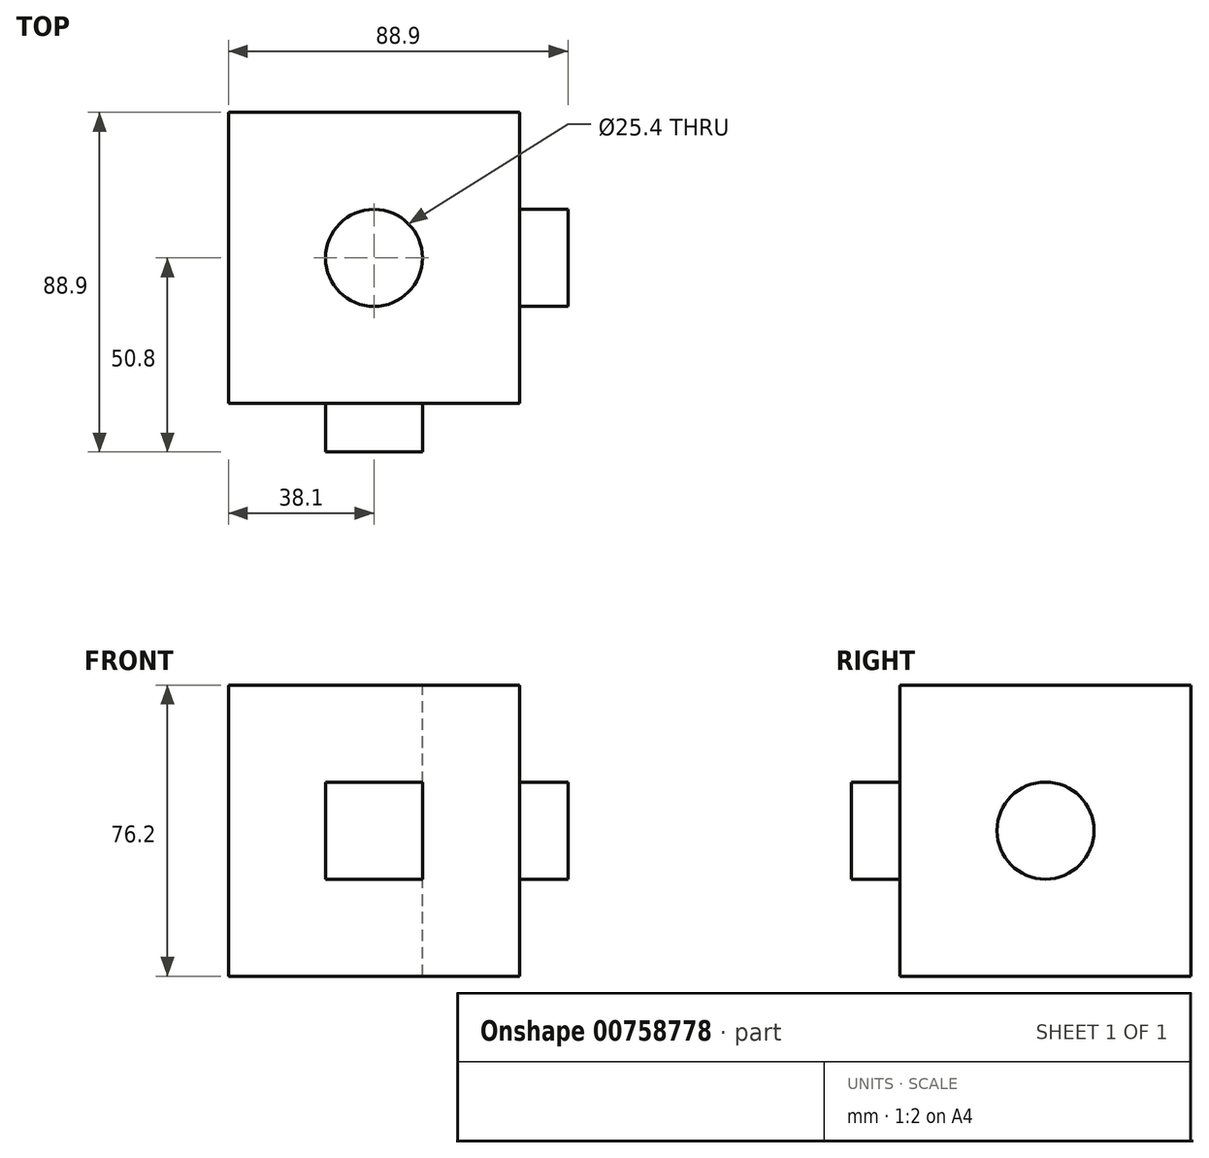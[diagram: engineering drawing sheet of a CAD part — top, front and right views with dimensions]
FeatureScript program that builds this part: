
annotation { "Feature Type Name" : "Feature", "Feature Type Description" : "" }
export const myFeature = defineFeature(function(context is Context, id is Id, definition is map)
    precondition{}
    {
        {
            var Q0;
            Q0=qCreatedBy(makeId("Front.planeOp"),FACE);
            var sketch = newSketch(context, id + "F0", { "sketchPlane" : qUnion([Q0])});
            skLineSegment(sketch, "E0.bottom", {"start": v(-36.95, 54.33) * mm, "end": v(39.25, 54.33) * mm});
            skLineSegment(sketch, "E0.top", {"start": v(-36.95, -21.87) * mm, "end": v(39.25, -21.87) * mm});
            skLineSegment(sketch, "E0.left", {"start": v(-36.95, 54.33) * mm, "end": v(-36.95, -21.87) * mm});
            skLineSegment(sketch, "E0.right", {"start": v(39.25, 54.33) * mm, "end": v(39.25, -21.87) * mm});
            skLineSegment(sketch, "E1.bottom", {"start": v(39.25, -21.87) * mm, "end": v(42.06, -21.87) * mm});
            skLineSegment(sketch, "E1.top", {"start": v(39.25, -18.33) * mm, "end": v(42.06, -18.33) * mm});
            skLineSegment(sketch, "E1.left", {"start": v(39.25, -21.87) * mm, "end": v(39.25, -18.33) * mm});
            skLineSegment(sketch, "E1.right", {"start": v(42.06, -21.87) * mm, "end": v(42.06, -18.33) * mm});
            skSolve(sketch);
        }
        {
            var Q0;
            Q0=makeQuery(id+"F0.imprint","IMPRINT",FACE,{"disambiguationData":[TD([[makeQuery(id+"F0.imprint","IMPRINT",EDGE,{"derivedFrom":sQuery(id+"F0.wireOp",EDGE,"E0.bottom")}),-1.0]])]});
            extrude(context, id + "F1", {"entities" : qUnion([Q0]), "depth" : 76.2 * mm, "offsetDistance" : 25.4 * mm});
        }
        {
            var Q0;
            Q0=makeQuery(id+"F1.opExtrude","CAP_FACE",FACE,{"disambiguationData":[OSD([sQuery(id+"F0.wireOp",EDGE,"E0.bottom"),sQuery(id+"F0.wireOp",EDGE,"E0.top"),sQuery(id+"F0.wireOp",EDGE,"E0.left"),sQuery(id+"F0.wireOp",EDGE,"E0.right"),sQuery(id+"F0.wireOp",EDGE,"E1.left")])],"isStart":false});
            var sketch = newSketch(context, id + "F2", { "sketchPlane" : qUnion([Q0])});
            skLineSegment(sketch, "E2.bottom", {"start": v(-11.55, 28.93) * mm, "end": v(13.85, 28.93) * mm});
            skLineSegment(sketch, "E2.top", {"start": v(-11.55, 3.53) * mm, "end": v(13.85, 3.53) * mm});
            skLineSegment(sketch, "E2.left", {"start": v(-11.55, 28.93) * mm, "end": v(-11.55, 3.53) * mm});
            skLineSegment(sketch, "E2.right", {"start": v(13.85, 28.93) * mm, "end": v(13.85, 3.53) * mm});
            skSolve(sketch);
        }
        {
            var Q0;
            Q0=makeQuery(id+"F2.imprint","IMPRINT",FACE,{"disambiguationData":[TD([[makeQuery(id+"F2.imprint","IMPRINT",EDGE,{"derivedFrom":sQuery(id+"F2.wireOp",EDGE,"E2.bottom")}),-1.0]])]});
            extrude(context, id + "F3", {"entities" : qUnion([Q0]), "operationType" : NewBodyOperationType.ADD, "depth" : 12.7 * mm, "offsetDistance" : 25.4 * mm});
        }
        {
            var Q0;
            Q0=makeQuery(id+"F1.opExtrude","SWEPT_FACE",FACE,{"disambiguationData":[OSD([sQuery(id+"F0.wireOp",EDGE,"E0.right"),sQuery(id+"F0.wireOp",EDGE,"E1.left")])]});
            var sketch = newSketch(context, id + "F4", { "sketchPlane" : qUnion([Q0])});
            skCircle(sketch, "E3", {"center": v(-38.1, 16.23) * mm, "radius": 12.7 * mm});
            skSolve(sketch);
        }
        {
            var Q0;
            Q0=makeQuery(id+"F4.imprint","IMPRINT",FACE,{"disambiguationData":[TD([[makeQuery(id+"F4.imprint","IMPRINT",EDGE,{"derivedFrom":sQuery(id+"F4.wireOp",EDGE,"E3")}),1.0]])]});
            extrude(context, id + "F5", {"entities" : qUnion([Q0]), "operationType" : NewBodyOperationType.ADD, "depth" : 12.7 * mm, "offsetDistance" : 25.4 * mm});
        }
        {
            var Q0;
            Q0=makeQuery(id+"F1.opExtrude","SWEPT_FACE",FACE,{"disambiguationData":[OSD([sQuery(id+"F0.wireOp",EDGE,"E0.bottom")])]});
            var sketch = newSketch(context, id + "F6", { "sketchPlane" : qUnion([Q0])});
            skPoint(sketch, "E4", {"position": v(1.15, -38.1) * mm});
            skSolve(sketch);
        }
        {
            var Q0;
            Q0=sQuery(id+"F6.wireOp",VERTEX,"E4");
            var Q1;
            Q1=makeQuery(id+"F1.opExtrude","SWEPT_BODY",BODY,{"disambiguationData":[OSD([sQuery(id+"F0.wireOp",EDGE,"E0.bottom"),sQuery(id+"F0.wireOp",EDGE,"E0.top"),sQuery(id+"F0.wireOp",EDGE,"E0.left"),sQuery(id+"F0.wireOp",EDGE,"E0.right"),sQuery(id+"F0.wireOp",EDGE,"E1.left")])]});
            hole(context, id + "F7", {"style" : HoleStyle.SIMPLE, "endStyle" : HoleEndStyle.THROUGH, "holeDiameter" : 25.4 * mm, "majorDiameter" : 6.35 * mm, "isTappedThrough" : true, "tappedDepth" : 12.7 * mm, "tapClearance" : 3, "locations" : qUnion([Q0]), "scope" : qUnion([Q1])});
        }
    });
